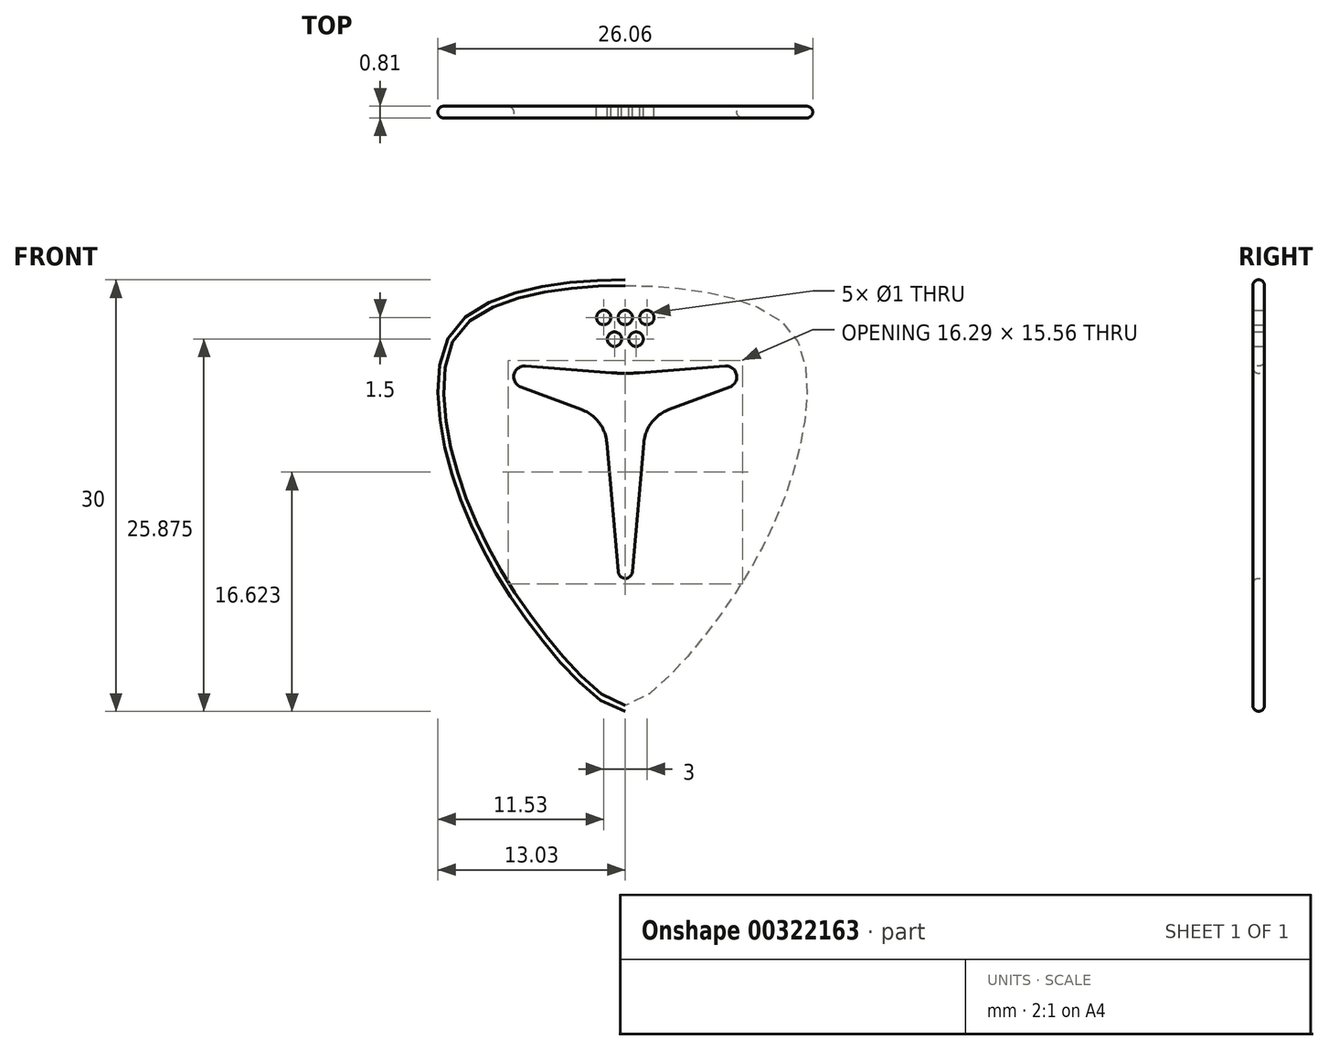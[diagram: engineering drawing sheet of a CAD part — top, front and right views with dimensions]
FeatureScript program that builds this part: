
annotation { "Feature Type Name" : "Feature", "Feature Type Description" : "" }
export const myFeature = defineFeature(function(context is Context, id is Id, definition is map)
    precondition{}
    {
        {
            var Q0;
            Q0=qCreatedBy(makeId("Front.planeOp"),FACE);
            var sketch = newSketch(context, id + "F0", { "sketchPlane" : qUnion([Q0])});
            skLineSegment(sketch, "E0", {"start": v(0, 0) * mm, "end": v(0, 6.75) * mm, "construction": true});
            skLineSegment(sketch, "E1", {"start": v(0, 0) * mm, "end": v(0, -23.25) * mm, "construction": true});
            skLineSegment(sketch, "E2", {"start": v(0, 0) * mm, "end": v(13, 0) * mm, "construction": true});
            skFitSpline(sketch, "E3", {"points": [v(0, -23.25) * mm, v(9.5, -12.75) * mm, v(13, 0) * mm, v(11, 4.25) * mm, v(0, 6.75) * mm], "startDerivative": vector(20.6, 0) * mm, "endDerivative": vector(-57.72, 0) * mm});
            skFitSpline(sketch, "E4.MirrorCS", {"points": [v(0, -23.25) * mm, v(-9.5, -12.75) * mm, v(-13, 0) * mm, v(-11, 4.25) * mm, v(0, 6.75) * mm], "startDerivative": vector(-20.6, 0) * mm, "endDerivative": vector(57.72, 0) * mm});
            skArc(sketch, "E5", {"start": v(7.26, -0.7) * mm, "mid": v(7.73, 0.16) * mm, "end": v(6.94, 0.75) * mm});
            skLineSegment(sketch, "E6", {"start": v(7.26, -0.7) * mm, "end": v(3.04, -2.27) * mm});
            skArc(sketch, "E7", {"start": v(3.04, -2.27) * mm, "mid": v(1.83, -3.17) * mm, "end": v(1.28, -4.58) * mm});
            skLineSegment(sketch, "E8", {"start": v(0.5, -13.54) * mm, "end": v(1.28, -4.58) * mm});
            skArc(sketch, "E9", {"start": v(0, -14) * mm, "mid": v(0.34, -13.87) * mm, "end": v(0.5, -13.54) * mm});
            skArc(sketch, "E10.MirrorCS", {"start": v(0, -14) * mm, "mid": v(-0.34, -13.87) * mm, "end": v(-0.5, -13.54) * mm});
            skLineSegment(sketch, "E11.MirrorCS", {"start": v(-0.5, -13.54) * mm, "end": v(-1.28, -4.58) * mm});
            skArc(sketch, "E12.MirrorCS", {"start": v(-3.04, -2.27) * mm, "mid": v(-1.83, -3.17) * mm, "end": v(-1.28, -4.58) * mm});
            skLineSegment(sketch, "E13.MirrorCS", {"start": v(-7.26, -0.7) * mm, "end": v(-3.04, -2.27) * mm});
            skArc(sketch, "E14.MirrorCS", {"start": v(-7.26, -0.7) * mm, "mid": v(-7.73, 0.16) * mm, "end": v(-6.94, 0.75) * mm});
            skLineSegment(sketch, "E15", {"start": v(6.94, 0.75) * mm, "end": v(0.96, 0.29) * mm});
            skArc(sketch, "E16", {"start": v(0, 0.25) * mm, "mid": v(0.48, 0.26) * mm, "end": v(0.96, 0.29) * mm});
            skArc(sketch, "E17.MirrorCS", {"start": v(0, 0.25) * mm, "mid": v(-0.48, 0.26) * mm, "end": v(-0.96, 0.29) * mm});
            skLineSegment(sketch, "E18.MirrorCS", {"start": v(-6.94, 0.75) * mm, "end": v(-0.96, 0.29) * mm});
            skLineSegment(sketch, "E19", {"start": v(0, 4.12) * mm, "end": v(1.5, 4.12) * mm, "construction": true});
            skCircle(sketch, "E20", {"center": v(0, 4.12) * mm, "radius": 0.5 * mm});
            skCircle(sketch, "E21", {"center": v(1.5, 4.12) * mm, "radius": 0.5 * mm});
            skCircle(sketch, "E22", {"center": v(0.75, 2.62) * mm, "radius": 0.5 * mm});
            skLineSegment(sketch, "E23", {"start": v(0.75, 2.62) * mm, "end": v(0, 2.62) * mm, "construction": true});
            skCircle(sketch, "E24.MirrorC", {"center": v(-1.5, 4.12) * mm, "radius": 0.5 * mm});
            skLineSegment(sketch, "E25.MirrorCS", {"start": v(0, 4.12) * mm, "end": v(-1.5, 4.12) * mm, "construction": true});
            skLineSegment(sketch, "E26.MirrorCS", {"start": v(-0.75, 2.62) * mm, "end": v(0, 2.62) * mm, "construction": true});
            skCircle(sketch, "E27.MirrorC", {"center": v(-0.75, 2.62) * mm, "radius": 0.5 * mm});
            skPoint(sketch, "E28", {"position": v(0, 3.38) * mm});
            skSolve(sketch);
        }
        {
            var Q0;
            Q0=qSketchRegion(id+"F0",true);
            extrude(context, id + "F1", {"entities" : qUnion([Q0]), "depth" : 0.81 * mm});
        }
        {
            var Q0;
            Q0=makeQuery(id+"F1.opExtrude","CAP_EDGE",EDGE,{"disambiguationData":[OSD([sQuery(id+"F0.wireOp",EDGE,"E5")])],"isStart":false});
            var Q1;
            Q1=makeQuery(id+"F1.opExtrude","CAP_EDGE",EDGE,{"disambiguationData":[OSD([sQuery(id+"F0.wireOp",EDGE,"E7")])],"isStart":true});
            var Q2;
            Q2=makeQuery(id+"F1.opExtrude","CAP_EDGE",EDGE,{"disambiguationData":[OSD([sQuery(id+"F0.wireOp",EDGE,"E9"),sQuery(id+"F0.wireOp",EDGE,"E10.MirrorCS")])],"isStart":false});
            var Q3;
            Q3=makeQuery(id+"F1.opExtrude","CAP_EDGE",EDGE,{"disambiguationData":[OSD([sQuery(id+"F0.wireOp",EDGE,"E14.MirrorCS")])],"isStart":false});
            var Q4;
            Q4=makeQuery(id+"F1.opExtrude","CAP_EDGE",EDGE,{"disambiguationData":[OSD([sQuery(id+"F0.wireOp",EDGE,"E5")])],"isStart":true});
            var Q5;
            Q5=makeQuery(id+"F1.opExtrude","CAP_EDGE",EDGE,{"disambiguationData":[OSD([sQuery(id+"F0.wireOp",EDGE,"E12.MirrorCS")])],"isStart":false});
            var Q6;
            Q6=makeQuery(id+"F1.opExtrude","CAP_EDGE",EDGE,{"disambiguationData":[OSD([sQuery(id+"F0.wireOp",EDGE,"E7")])],"isStart":false});
            var Q7;
            Q7=makeQuery(id+"F1.opExtrude","CAP_EDGE",EDGE,{"disambiguationData":[OSD([sQuery(id+"F0.wireOp",EDGE,"cP70XH3B-hxny-nh1n-TbyW-52Zl4TOD4HrO"),sQuery(id+"F0.wireOp",EDGE,"9cf6c757-e815-40dd-95a7-672993b90d513.MirrorCS")])],"isStart":true});
            var Q8;
            Q8=makeQuery(id+"F1.opExtrude","CAP_EDGE",EDGE,{"disambiguationData":[OSD([sQuery(id+"F0.wireOp",EDGE,"E13.MirrorCS")])],"isStart":false});
            var Q9;
            Q9=makeQuery(id+"F1.opExtrude","CAP_EDGE",EDGE,{"disambiguationData":[OSD([sQuery(id+"F0.wireOp",EDGE,"E12.MirrorCS")])],"isStart":true});
            var Q10;
            Q10=makeQuery(id+"F1.opExtrude","CAP_EDGE",EDGE,{"disambiguationData":[OSD([sQuery(id+"F0.wireOp",EDGE,"cP70XH3B-hxny-nh1n-TbyW-52Zl4TOD4HrO"),sQuery(id+"F0.wireOp",EDGE,"9cf6c757-e815-40dd-95a7-672993b90d513.MirrorCS")])],"isStart":false});
            var Q11;
            Q11=makeQuery(id+"F1.opExtrude","CAP_EDGE",EDGE,{"disambiguationData":[OSD([sQuery(id+"F0.wireOp",EDGE,"E9"),sQuery(id+"F0.wireOp",EDGE,"E10.MirrorCS")])],"isStart":true});
            var Q12;
            Q12=makeQuery(id+"F1.opExtrude","SWEPT_EDGE",EDGE,{"disambiguationData":[OSD([sQuery(id+"F0.wireOp",EDGE,"9cf6c757-e815-40dd-95a7-672993b90d513.MirrorCS"),sQuery(id+"F0.wireOp",EDGE,"E14.MirrorCS")])]});
            var Q13;
            Q13=makeQuery(id+"F1.opExtrude","CAP_EDGE",EDGE,{"disambiguationData":[OSD([sQuery(id+"F0.wireOp",EDGE,"E8")])],"isStart":true});
            var Q14;
            Q14=makeQuery(id+"F1.opExtrude","CAP_EDGE",EDGE,{"disambiguationData":[OSD([sQuery(id+"F0.wireOp",EDGE,"E11.MirrorCS")])],"isStart":false});
            var Q15;
            Q15=makeQuery(id+"F1.opExtrude","SWEPT_EDGE",EDGE,{"disambiguationData":[OSD([sQuery(id+"F0.wireOp",EDGE,"E6"),sQuery(id+"F0.wireOp",EDGE,"E7")])]});
            var Q16;
            Q16=makeQuery(id+"F1.opExtrude","SWEPT_EDGE",EDGE,{"disambiguationData":[OSD([sQuery(id+"F0.wireOp",EDGE,"E8"),sQuery(id+"F0.wireOp",EDGE,"E9")])]});
            var Q17;
            Q17=makeQuery(id+"F1.opExtrude","SWEPT_EDGE",EDGE,{"disambiguationData":[OSD([sQuery(id+"F0.wireOp",EDGE,"E13.MirrorCS"),sQuery(id+"F0.wireOp",EDGE,"E14.MirrorCS")])]});
            var Q18;
            Q18=makeQuery(id+"F1.opExtrude","SWEPT_EDGE",EDGE,{"disambiguationData":[OSD([sQuery(id+"F0.wireOp",EDGE,"E10.MirrorCS"),sQuery(id+"F0.wireOp",EDGE,"E11.MirrorCS")])]});
            var Q19;
            Q19=makeQuery(id+"F1.opExtrude","SWEPT_EDGE",EDGE,{"disambiguationData":[OSD([sQuery(id+"F0.wireOp",EDGE,"E11.MirrorCS"),sQuery(id+"F0.wireOp",EDGE,"E12.MirrorCS")])]});
            var Q20;
            Q20=makeQuery(id+"F1.opExtrude","SWEPT_EDGE",EDGE,{"disambiguationData":[OSD([sQuery(id+"F0.wireOp",EDGE,"E5"),sQuery(id+"F0.wireOp",EDGE,"E6")])]});
            var Q21;
            Q21=makeQuery(id+"F1.opExtrude","CAP_EDGE",EDGE,{"disambiguationData":[OSD([sQuery(id+"F0.wireOp",EDGE,"E14.MirrorCS")])],"isStart":true});
            var Q22;
            Q22=makeQuery(id+"F1.opExtrude","SWEPT_EDGE",EDGE,{"disambiguationData":[OSD([sQuery(id+"F0.wireOp",EDGE,"E12.MirrorCS"),sQuery(id+"F0.wireOp",EDGE,"E13.MirrorCS")])]});
            var Q23;
            Q23=makeQuery(id+"F1.opExtrude","CAP_EDGE",EDGE,{"disambiguationData":[OSD([sQuery(id+"F0.wireOp",EDGE,"E8")])],"isStart":false});
            var Q24;
            Q24=makeQuery(id+"F1.opExtrude","SWEPT_EDGE",EDGE,{"disambiguationData":[OSD([sQuery(id+"F0.wireOp",EDGE,"cP70XH3B-hxny-nh1n-TbyW-52Zl4TOD4HrO"),sQuery(id+"F0.wireOp",EDGE,"E5")])]});
            var Q25;
            Q25=makeQuery(id+"F1.opExtrude","CAP_EDGE",EDGE,{"disambiguationData":[OSD([sQuery(id+"F0.wireOp",EDGE,"E6")])],"isStart":false});
            var Q26;
            Q26=makeQuery(id+"F1.opExtrude","CAP_EDGE",EDGE,{"disambiguationData":[OSD([sQuery(id+"F0.wireOp",EDGE,"E11.MirrorCS")])],"isStart":true});
            var Q27;
            Q27=makeQuery(id+"F1.opExtrude","SWEPT_EDGE",EDGE,{"disambiguationData":[OSD([sQuery(id+"F0.wireOp",EDGE,"E7"),sQuery(id+"F0.wireOp",EDGE,"E8")])]});
            var Q28;
            Q28=makeQuery(id+"F1.opExtrude","CAP_EDGE",EDGE,{"disambiguationData":[OSD([sQuery(id+"F0.wireOp",EDGE,"E6")])],"isStart":true});
            var Q29;
            Q29=makeQuery(id+"F1.opExtrude","CAP_EDGE",EDGE,{"disambiguationData":[OSD([sQuery(id+"F0.wireOp",EDGE,"E13.MirrorCS")])],"isStart":true});
            var Q30;
            Q30=makeQuery(id+"F1.opExtrude","CAP_EDGE",EDGE,{"disambiguationData":[OSD([sQuery(id+"F0.wireOp",EDGE,"E18.MirrorCS")])],"isStart":false});
            var Q31;
            Q31=makeQuery(id+"F1.opExtrude","CAP_EDGE",EDGE,{"disambiguationData":[OSD([sQuery(id+"F0.wireOp",EDGE,"E18.MirrorCS")])],"isStart":true});
            var Q32;
            Q32=makeQuery(id+"F1.opExtrude","CAP_EDGE",EDGE,{"disambiguationData":[OSD([sQuery(id+"F0.wireOp",EDGE,"E16"),sQuery(id+"F0.wireOp",EDGE,"E17.MirrorCS")])],"isStart":false});
            var Q33;
            Q33=makeQuery(id+"F1.opExtrude","CAP_EDGE",EDGE,{"disambiguationData":[OSD([sQuery(id+"F0.wireOp",EDGE,"E16"),sQuery(id+"F0.wireOp",EDGE,"E17.MirrorCS")])],"isStart":true});
            var Q34;
            Q34=makeQuery(id+"F1.opExtrude","CAP_EDGE",EDGE,{"disambiguationData":[OSD([sQuery(id+"F0.wireOp",EDGE,"E15")])],"isStart":false});
            var Q35;
            Q35=makeQuery(id+"F1.opExtrude","CAP_EDGE",EDGE,{"disambiguationData":[OSD([sQuery(id+"F0.wireOp",EDGE,"E15")])],"isStart":true});
            fillet(context, id + "F2", {"entities" : qUnion([Q0, Q1, Q2, Q3, Q4, Q5, Q6, Q7, Q8, Q9, Q10, Q11, Q12, Q13, Q14, Q15, Q16, Q17, Q18, Q19, Q20, Q21, Q22, Q23, Q24, Q25, Q26, Q27, Q28, Q29, Q30, Q31, Q32, Q33, Q34, Q35]), "radius" : (0.81 / 2) * mm, "tangentPropagation" : true, "allowEdgeOverflow" : false});
        }
        {
            var Q0;
            Q0=makeQuery(id+"F1.opExtrude","CAP_EDGE",EDGE,{"disambiguationData":[OSD([sQuery(id+"F0.wireOp",EDGE,"E4.MirrorCS")])],"isStart":false});
            var Q1;
            Q1=makeQuery(id+"F1.opExtrude","CAP_EDGE",EDGE,{"disambiguationData":[OSD([sQuery(id+"F0.wireOp",EDGE,"E3")])],"isStart":false});
            var Q2;
            Q2=makeQuery(id+"F1.opExtrude","CAP_EDGE",EDGE,{"disambiguationData":[OSD([sQuery(id+"F0.wireOp",EDGE,"E4.MirrorCS")])],"isStart":true});
            var Q3;
            Q3=makeQuery(id+"F1.opExtrude","CAP_EDGE",EDGE,{"disambiguationData":[OSD([sQuery(id+"F0.wireOp",EDGE,"E3")])],"isStart":true});
            fillet(context, id + "F3", {"entities" : qUnion([Q0, Q1, Q2, Q3]), "radius" : 0.81 / 2 * mm, "tangentPropagation" : true, "allowEdgeOverflow" : false});
        }
    });
